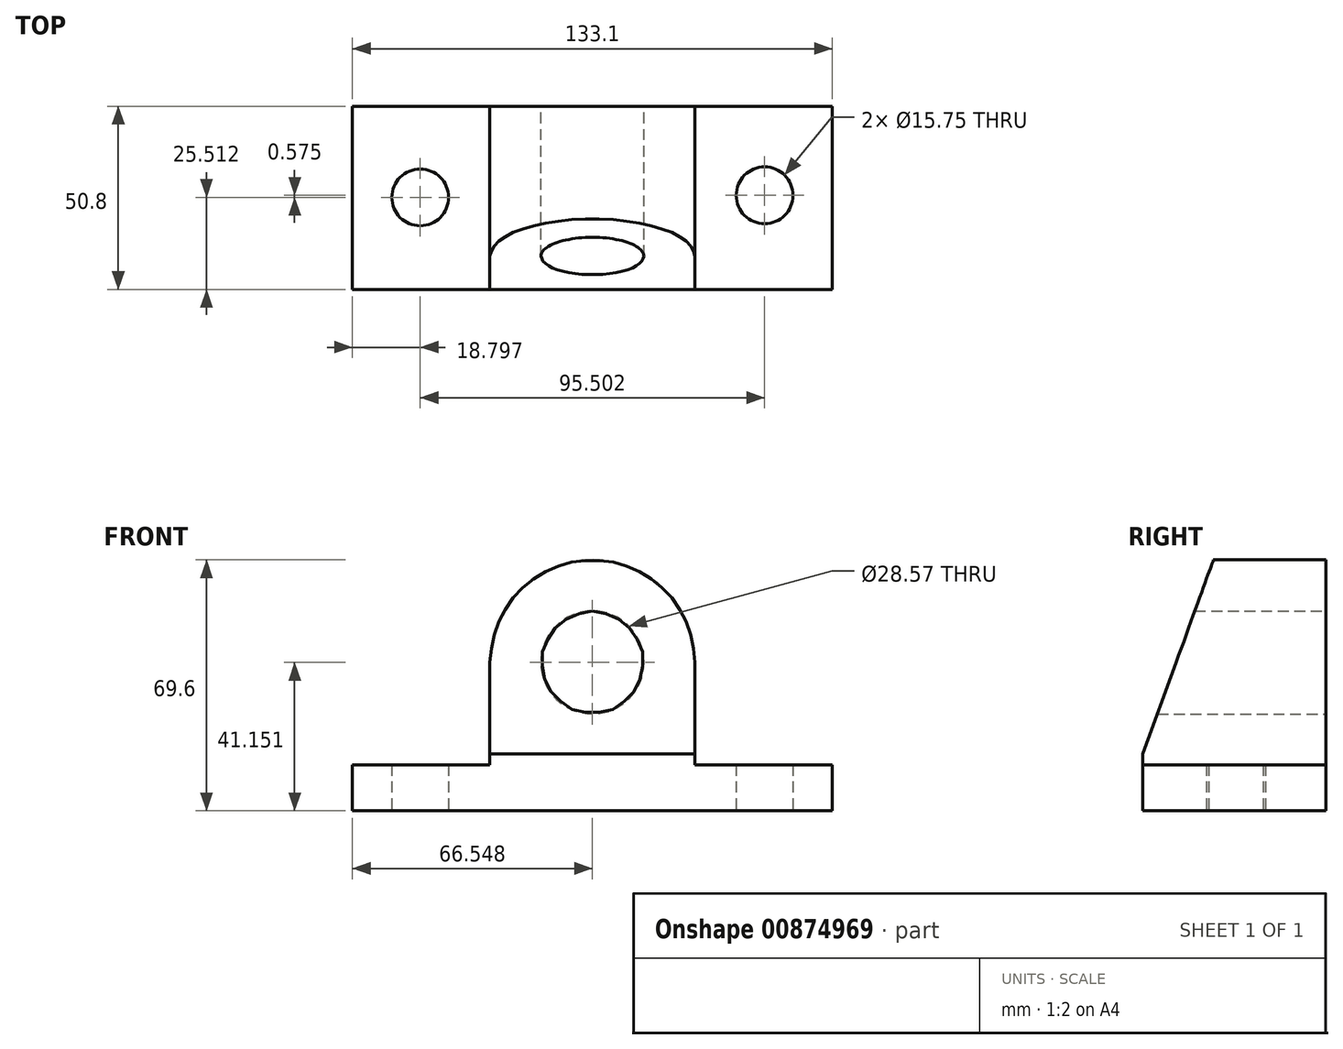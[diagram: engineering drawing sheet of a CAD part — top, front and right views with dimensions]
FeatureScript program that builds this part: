
annotation { "Feature Type Name" : "Feature", "Feature Type Description" : "" }
export const myFeature = defineFeature(function(context is Context, id is Id, definition is map)
    precondition{}
    {
        {
            var Q0;
            Q0=qCreatedBy(makeId("Right.planeOp"),FACE);
            var sketch = newSketch(context, id + "F0", { "sketchPlane" : qUnion([Q0])});
            skLineSegment(sketch, "E0.bottom", {"start": v(-6.6, 14.82) * mm, "end": v(24.6, 14.82) * mm});
            skLineSegment(sketch, "E0.top", {"start": v(-26.2, -54.78) * mm, "end": v(24.6, -54.78) * mm});
            skLineSegment(sketch, "E0.left", {"start": v(-26.2, -39.03) * mm, "end": v(-26.2, -54.78) * mm});
            skLineSegment(sketch, "E0.right", {"start": v(24.6, 14.82) * mm, "end": v(24.6, -54.78) * mm});
            skLineSegment(sketch, "E1", {"start": v(-26.2, -54.78) * mm, "end": v(-26.2, -39.03) * mm});
            skLineSegment(sketch, "E2", {"start": v(-26.2, -39.03) * mm, "end": v(24.6, -39.03) * mm});
            skLineSegment(sketch, "E3", {"start": v(-26.2, -39.03) * mm, "end": v(-6.6, 14.82) * mm});
            skSolve(sketch);
        }
        {
            var Q0;
            Q0=qSketchRegion(id+"F0",true);
            extrude(context, id + "F1", {"entities" : qUnion([Q0]), "depth" : 133.1 * mm, "offsetDistance" : 25.4 * mm});
        }
        {
            var Q0;
            Q0=makeQuery(id+"F1.opExtrude","SWEPT_FACE",FACE,{"disambiguationData":[OSD([sQuery(id+"F0.wireOp",EDGE,"E0.right")])]});
            var sketch = newSketch(context, id + "F2", { "sketchPlane" : qUnion([Q0])});
            skLineSegment(sketch, "E4", {"start": v(-133.1, -54.78) * mm, "end": v(-133.1, -42.08) * mm});
            skLineSegment(sketch, "E5", {"start": v(-133.1, -42.08) * mm, "end": v(-95, -42.08) * mm});
            skLineSegment(sketch, "E6", {"start": v(0, -42.08) * mm, "end": v(-38.1, -42.08) * mm});
            skArc(sketch, "E7", {"start": v(-38.1, -13.63) * mm, "mid": v(-66.55, 14.82) * mm, "end": v(-95, -13.63) * mm});
            skCircle(sketch, "E8", {"center": v(-66.55, -13.63) * mm, "radius": 14.29 * mm});
            skLineSegment(sketch, "E9", {"start": v(-95, -13.63) * mm, "end": v(-95, -42.08) * mm});
            skLineSegment(sketch, "E10", {"start": v(-38.1, -13.63) * mm, "end": v(-38.1, -42.08) * mm});
            skPoint(sketch, "E11.orphan", {"position": v(-66.55, 14.82) * mm});
            skLineSegment(sketch, "E12.trimOffspring", {"start": v(-38.1, -42.08) * mm, "end": v(0, -42.08) * mm});
            skLineSegment(sketch, "E13", {"start": v(-133.1, -54.78) * mm, "end": v(0, -54.78) * mm});
            skLineSegment(sketch, "E14", {"start": v(0, -54.78) * mm, "end": v(0, -42.08) * mm});
            skSolve(sketch);
        }
        {
            var Q0;
            {var subQ7=sQuery(id+"F2.wireOp",EDGE,"E5");Q0=makeQuery(id+"F2.imprint","IMPRINT",FACE,{"disambiguationData":[TD([[makeQuery(id+"F2.imprint","IMPRINT",EDGE,{"derivedFrom":subQ7}),1.0]])]});}
            var Q1;
            {var subQ5=sQuery(id+"F2.wireOp",EDGE,"E10");Q1=makeQuery(id+"F2.imprint","IMPRINT",FACE,{"disambiguationData":[TD([[makeQuery(id+"F2.imprint","IMPRINT",EDGE,{"derivedFrom":subQ5}),1.0]])]});}
            var Q2;
            Q2=makeQuery(id+"F2.imprint","IMPRINT",FACE,{"disambiguationData":[TD([[makeQuery(id+"F2.imprint","IMPRINT",EDGE,{"derivedFrom":sQuery(id+"F2.wireOp",EDGE,"E8")}),1.0]])]});
            extrude(context, id + "F3", {"entities" : qUnion([Q0, Q1, Q2]), "operationType" : NewBodyOperationType.REMOVE, "oppositeDirection" : true, "depth" : 50.8 * mm, "offsetDistance" : 25.4 * mm});
        }
        {
            var Q0;
            Q0=makeQuery(id+"F1.opExtrude","SWEPT_FACE",FACE,{"disambiguationData":[OSD([sQuery(id+"F0.wireOp",EDGE,"E0.top")])]});
            var sketch = newSketch(context, id + "F4", { "sketchPlane" : qUnion([Q0])});
            skLineSegment(sketch, "E15", {"start": v(0, 26.2) * mm, "end": v(0, 0.8) * mm});
            skCircle(sketch, "E16", {"center": v(18.8, 0.69) * mm, "radius": 7.87 * mm});
            skCircle(sketch, "E17", {"center": v(114.3, 0.11) * mm, "radius": 7.87 * mm});
            skPoint(sketch, "E18.end.orphan", {"position": v(66.7, 26.2) * mm});
            skPoint(sketch, "E19.orphan", {"position": v(66.55, 0.4) * mm});
            skPoint(sketch, "E20.start.orphan", {"position": v(133.1, 0) * mm});
            skSolve(sketch);
        }
        {
            var Q0;
            Q0=qSketchRegion(id+"F4",true);
            extrude(context, id + "F5", {"entities" : qUnion([Q0]), "operationType" : NewBodyOperationType.REMOVE, "oppositeDirection" : true, "depth" : 12.7 * mm, "offsetDistance" : 25.4 * mm});
        }
    });
